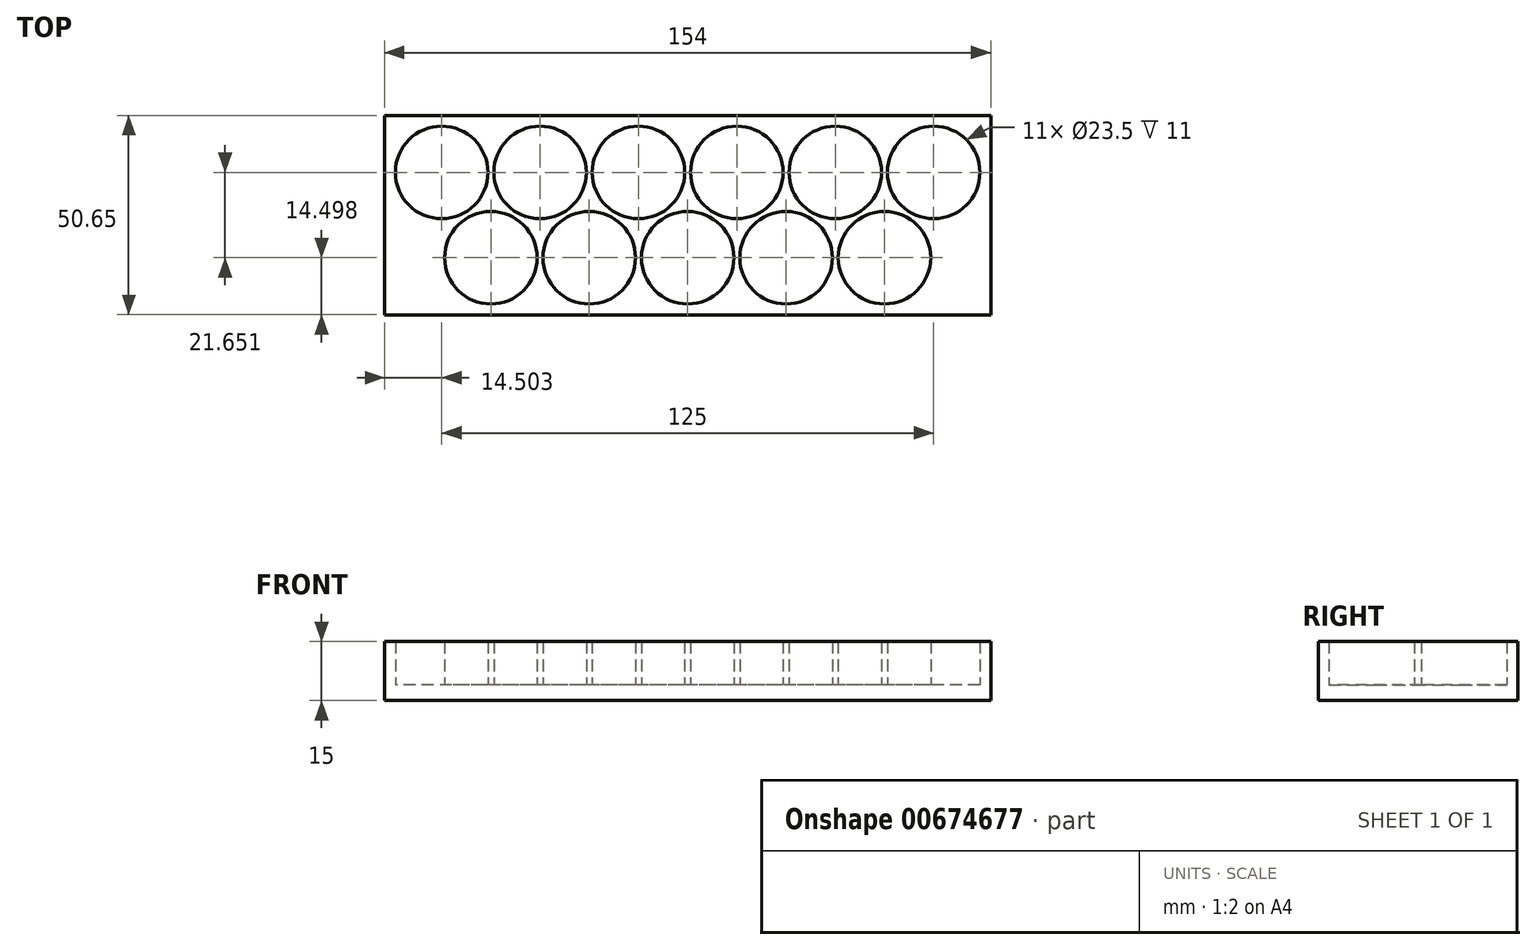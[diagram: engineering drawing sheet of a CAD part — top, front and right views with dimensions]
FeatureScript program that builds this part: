
annotation { "Feature Type Name" : "Feature", "Feature Type Description" : "" }
export const myFeature = defineFeature(function(context is Context, id is Id, definition is map)
    precondition{}
    {
        {
            var Q0;
            Q0=qCreatedBy(makeId("Top.planeOp"),FACE);
            var sketch = newSketch(context, id + "F0", { "sketchPlane" : qUnion([Q0])});
            skCircle(sketch, "E0", {"center": v(-65.26, 25.7) * mm, "radius": 11.75 * mm});
            skCircle(sketch, "E1.0.1.0", {"center": v(-77.76, 47.35) * mm, "radius": 11.75 * mm});
            skCircle(sketch, "E1.1.0.0", {"center": v(-40.26, 25.7) * mm, "radius": 11.75 * mm});
            skCircle(sketch, "E1.1.1.0", {"center": v(-52.76, 47.35) * mm, "radius": 11.75 * mm});
            skCircle(sketch, "E1.2.0.0", {"center": v(-15.26, 25.7) * mm, "radius": 11.75 * mm});
            skCircle(sketch, "E1.2.1.0", {"center": v(-27.76, 47.35) * mm, "radius": 11.75 * mm});
            skCircle(sketch, "E1.3.0.0", {"center": v(9.74, 25.7) * mm, "radius": 11.75 * mm});
            skCircle(sketch, "E1.3.1.0", {"center": v(-2.76, 47.35) * mm, "radius": 11.75 * mm});
            skCircle(sketch, "E1.4.0.0", {"center": v(34.74, 25.7) * mm, "radius": 11.75 * mm});
            skCircle(sketch, "E1.4.1.0", {"center": v(22.24, 47.35) * mm, "radius": 11.75 * mm});
            skLineSegment(sketch, "E1.direction1", {"start": v(-65.26, 25.7) * mm, "end": v(-40.26, 25.7) * mm, "construction": true});
            skLineSegment(sketch, "E1.direction2", {"start": v(-65.26, 25.7) * mm, "end": v(-77.76, 47.35) * mm, "construction": true});
            skCircle(sketch, "E2.0.5.1", {"center": v(47.24, 47.35) * mm, "radius": 11.75 * mm});
            skLineSegment(sketch, "E3.bottom", {"start": v(-92.26, 61.85) * mm, "end": v(61.74, 61.85) * mm});
            skLineSegment(sketch, "E3.top", {"start": v(-92.26, 11.2) * mm, "end": v(61.74, 11.2) * mm});
            skLineSegment(sketch, "E3.left", {"start": v(-92.26, 61.85) * mm, "end": v(-92.26, 11.2) * mm});
            skLineSegment(sketch, "E3.right", {"start": v(61.74, 61.85) * mm, "end": v(61.74, 11.2) * mm});
            skSolve(sketch);
        }
        {
            var Q0;
            Q0=makeQuery(id+"F0.imprint","IMPRINT",FACE,{"disambiguationData":[TD([[makeQuery(id+"F0.imprint","IMPRINT",EDGE,{"derivedFrom":sQuery(id+"F0.wireOp",EDGE,"E0")}),-1.0]])]});
            var Q1;
            Q1=makeQuery(id+"F0.imprint","IMPRINT",FACE,{"disambiguationData":[TD([[makeQuery(id+"F0.imprint","IMPRINT",EDGE,{"derivedFrom":sQuery(id+"F0.wireOp",EDGE,"E1.0.1.0")}),1.0]])]});
            var Q2;
            Q2=makeQuery(id+"F0.imprint","IMPRINT",FACE,{"disambiguationData":[TD([[makeQuery(id+"F0.imprint","IMPRINT",EDGE,{"derivedFrom":sQuery(id+"F0.wireOp",EDGE,"E0")}),1.0]])]});
            var Q3;
            Q3=makeQuery(id+"F0.imprint","IMPRINT",FACE,{"disambiguationData":[TD([[makeQuery(id+"F0.imprint","IMPRINT",EDGE,{"derivedFrom":sQuery(id+"F0.wireOp",EDGE,"E1.1.1.0")}),1.0]])]});
            var Q4;
            Q4=makeQuery(id+"F0.imprint","IMPRINT",FACE,{"disambiguationData":[TD([[makeQuery(id+"F0.imprint","IMPRINT",EDGE,{"derivedFrom":sQuery(id+"F0.wireOp",EDGE,"E1.1.0.0")}),1.0]])]});
            var Q5;
            Q5=makeQuery(id+"F0.imprint","IMPRINT",FACE,{"disambiguationData":[TD([[makeQuery(id+"F0.imprint","IMPRINT",EDGE,{"derivedFrom":sQuery(id+"F0.wireOp",EDGE,"E1.2.1.0")}),1.0]])]});
            var Q6;
            Q6=makeQuery(id+"F0.imprint","IMPRINT",FACE,{"disambiguationData":[TD([[makeQuery(id+"F0.imprint","IMPRINT",EDGE,{"derivedFrom":sQuery(id+"F0.wireOp",EDGE,"E1.3.1.0")}),1.0]])]});
            var Q7;
            Q7=makeQuery(id+"F0.imprint","IMPRINT",FACE,{"disambiguationData":[TD([[makeQuery(id+"F0.imprint","IMPRINT",EDGE,{"derivedFrom":sQuery(id+"F0.wireOp",EDGE,"E1.2.0.0")}),1.0]])]});
            var Q8;
            Q8=makeQuery(id+"F0.imprint","IMPRINT",FACE,{"disambiguationData":[TD([[makeQuery(id+"F0.imprint","IMPRINT",EDGE,{"derivedFrom":sQuery(id+"F0.wireOp",EDGE,"E1.3.0.0")}),1.0]])]});
            var Q9;
            Q9=makeQuery(id+"F0.imprint","IMPRINT",FACE,{"disambiguationData":[TD([[makeQuery(id+"F0.imprint","IMPRINT",EDGE,{"derivedFrom":sQuery(id+"F0.wireOp",EDGE,"E2.0.5.1")}),1.0]])]});
            var Q10;
            Q10=makeQuery(id+"F0.imprint","IMPRINT",FACE,{"disambiguationData":[TD([[makeQuery(id+"F0.imprint","IMPRINT",EDGE,{"derivedFrom":sQuery(id+"F0.wireOp",EDGE,"E1.4.0.0")}),1.0]])]});
            var Q11;
            Q11=makeQuery(id+"F0.imprint","IMPRINT",FACE,{"disambiguationData":[TD([[makeQuery(id+"F0.imprint","IMPRINT",EDGE,{"derivedFrom":sQuery(id+"F0.wireOp",EDGE,"E1.4.1.0")}),1.0]])]});
            extrude(context, id + "F1", {"entities" : qUnion([Q0, Q1, Q2, Q3, Q4, Q5, Q6, Q7, Q8, Q9, Q10, Q11]), "oppositeDirection" : true, "depth" : 4 * mm, "offsetDistance" : 25 * mm});
        }
        {
            var Q0;
            Q0=makeQuery(id+"F0.imprint","IMPRINT",FACE,{"disambiguationData":[TD([[makeQuery(id+"F0.imprint","IMPRINT",EDGE,{"derivedFrom":sQuery(id+"F0.wireOp",EDGE,"E0")}),-1.0]])]});
            extrude(context, id + "F2", {"entities" : qUnion([Q0]), "operationType" : NewBodyOperationType.ADD, "depth" : 11 * mm, "offsetDistance" : 25 * mm});
        }
    });
